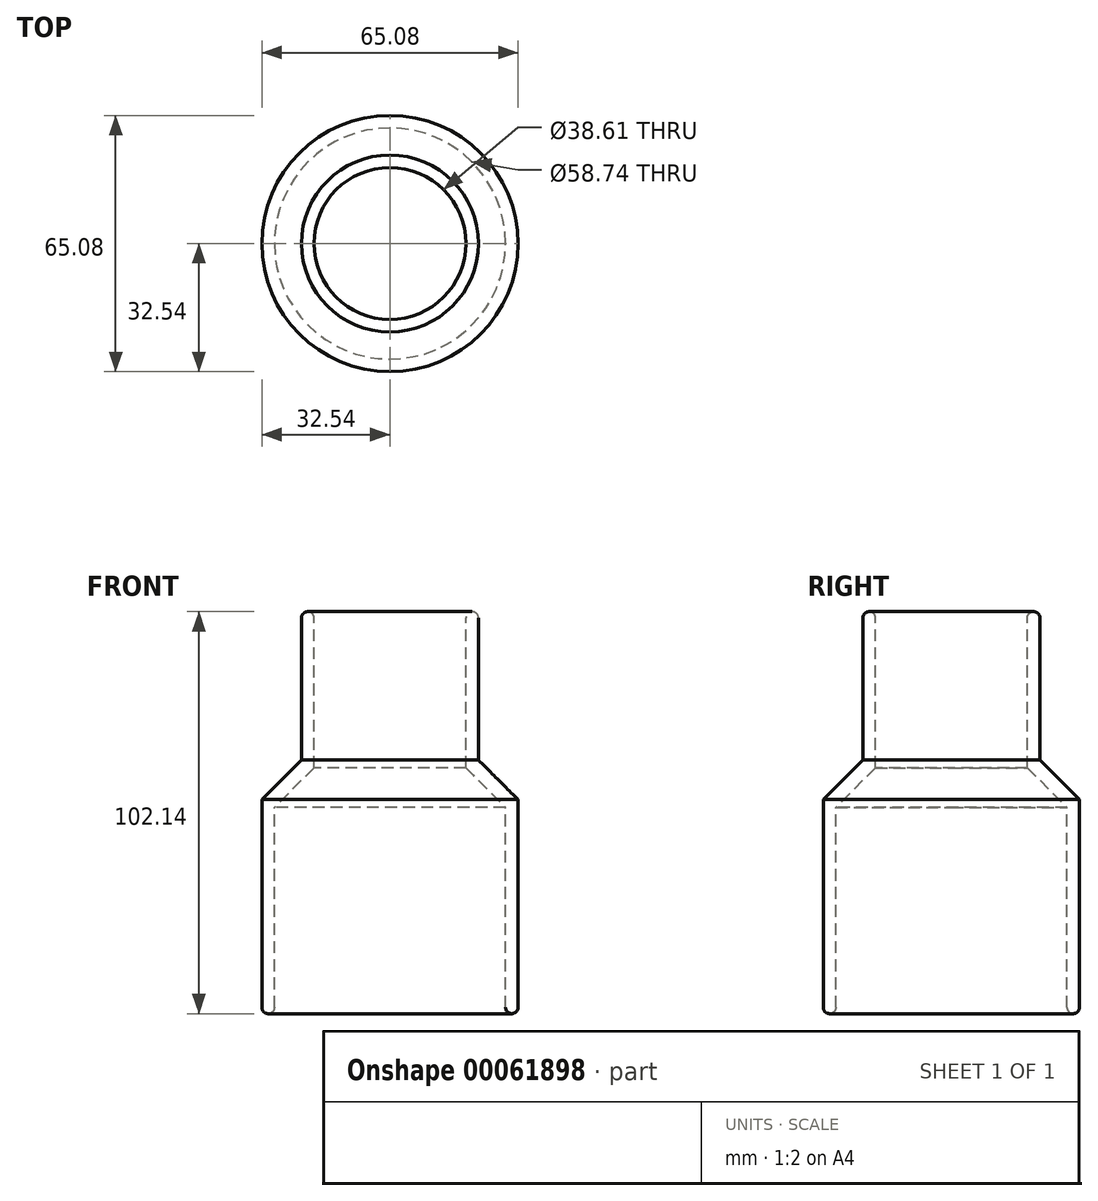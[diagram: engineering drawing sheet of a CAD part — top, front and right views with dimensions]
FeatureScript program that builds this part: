
annotation { "Feature Type Name" : "Feature", "Feature Type Description" : "" }
export const myFeature = defineFeature(function(context is Context, id is Id, definition is map)
    precondition{}
    {
        {
            var Q0;
            Q0=qCreatedBy(makeId("Front.planeOp"),FACE);
            var sketch = newSketch(context, id + "F0", { "sketchPlane" : qUnion([Q0])});
            skLineSegment(sketch, "E0", {"start": v(29.37, 1.59) * mm, "end": v(29.37, 52.39) * mm});
            skLineSegment(sketch, "E1", {"start": v(19.3, 62.45) * mm, "end": v(29.37, 52.39) * mm});
            skLineSegment(sketch, "E2", {"start": v(19.3, 62.45) * mm, "end": v(19.3, 100.55) * mm});
            skLineSegment(sketch, "E3.0", {"start": v(22.48, 64.46) * mm, "end": v(22.48, 100.55) * mm});
            skLineSegment(sketch, "E3.1", {"start": v(22.48, 64.46) * mm, "end": v(32.54, 54.4) * mm});
            skLineSegment(sketch, "E3.2", {"start": v(32.54, 1.59) * mm, "end": v(32.54, 54.4) * mm});
            skArc(sketch, "E4", {"start": v(22.48, 100.55) * mm, "mid": v(20.9, 102.14) * mm, "end": v(19.3, 100.55) * mm});
            skArc(sketch, "E5", {"start": v(29.37, 1.59) * mm, "mid": v(30.96, 0) * mm, "end": v(32.54, 1.59) * mm});
            skLineSegment(sketch, "E6", {"start": v(0, 56.78) * mm, "end": v(0, -13.5) * mm, "construction": true});
            skSolve(sketch);
        }
        {
            var Q0;
            Q0=makeQuery(id+"F0.imprint","IMPRINT",FACE,{"disambiguationData":[TD([[makeQuery(id+"F0.imprint","IMPRINT",EDGE,{"derivedFrom":sQuery(id+"F0.wireOp",EDGE,"E0")}),-1.0]])]});
            var Q1;
            Q1=sQuery(id+"F0.wireOp",EDGE,"E6");
            revolve(context, id + "F1", {"entities" : qUnion([Q0]), "axis" : qUnion([Q1]), "revolveType" : RevolveType.FULL});
        }
    });
